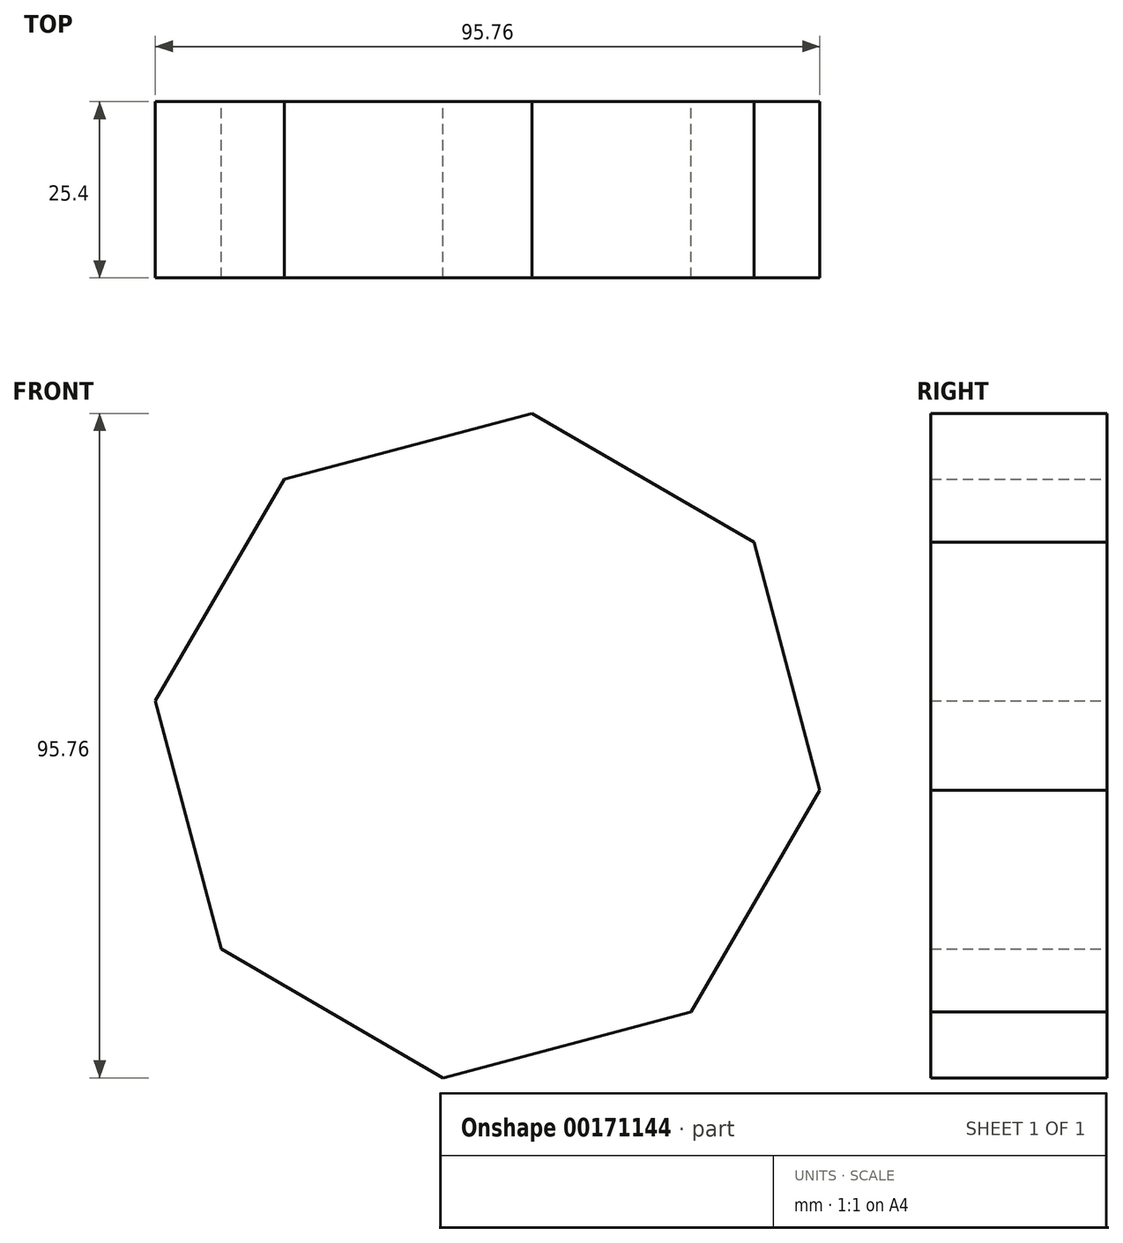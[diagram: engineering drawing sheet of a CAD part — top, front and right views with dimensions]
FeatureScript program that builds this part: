
annotation { "Feature Type Name" : "Feature", "Feature Type Description" : "" }
export const myFeature = defineFeature(function(context is Context, id is Id, definition is map)
    precondition{}
    {
        {
            var Q0;
            Q0=qCreatedBy(makeId("Front.planeOp"),FACE);
            var sketch = newSketch(context, id + "F0", { "sketchPlane" : qUnion([Q0])});
            skCircle(sketch, "E0.cCircle", {"center": v(0, 0) * mm, "radius": 44.63 * mm, "construction": true});
            skLineSegment(sketch, "E0.0", {"start": v(-47.88, 6.43) * mm, "end": v(-29.31, 38.4) * mm});
            skLineSegment(sketch, "E0.1", {"start": v(-29.31, 38.4) * mm, "end": v(6.43, 47.88) * mm});
            skLineSegment(sketch, "E0.2", {"start": v(6.43, 47.88) * mm, "end": v(38.4, 29.31) * mm});
            skLineSegment(sketch, "E0.3", {"start": v(38.4, 29.31) * mm, "end": v(47.88, -6.43) * mm});
            skLineSegment(sketch, "E0.4", {"start": v(47.88, -6.43) * mm, "end": v(29.31, -38.4) * mm});
            skLineSegment(sketch, "E0.5", {"start": v(29.31, -38.4) * mm, "end": v(-6.43, -47.88) * mm});
            skLineSegment(sketch, "E0.6", {"start": v(-6.43, -47.88) * mm, "end": v(-38.4, -29.31) * mm});
            skLineSegment(sketch, "E0.7", {"start": v(-38.4, -29.31) * mm, "end": v(-47.88, 6.43) * mm});
            skPoint(sketch, "E0.0.midPoint", {"position": v(-38.6, 22.41) * mm});
            skSolve(sketch);
        }
        {
            var Q0;
            Q0 = qSketchRegion(id + "F0", true);
            extrude(context, id + "F1", {"entities" : qUnion([Q0]), "depth" : 25.4 * mm});
        }
    });
